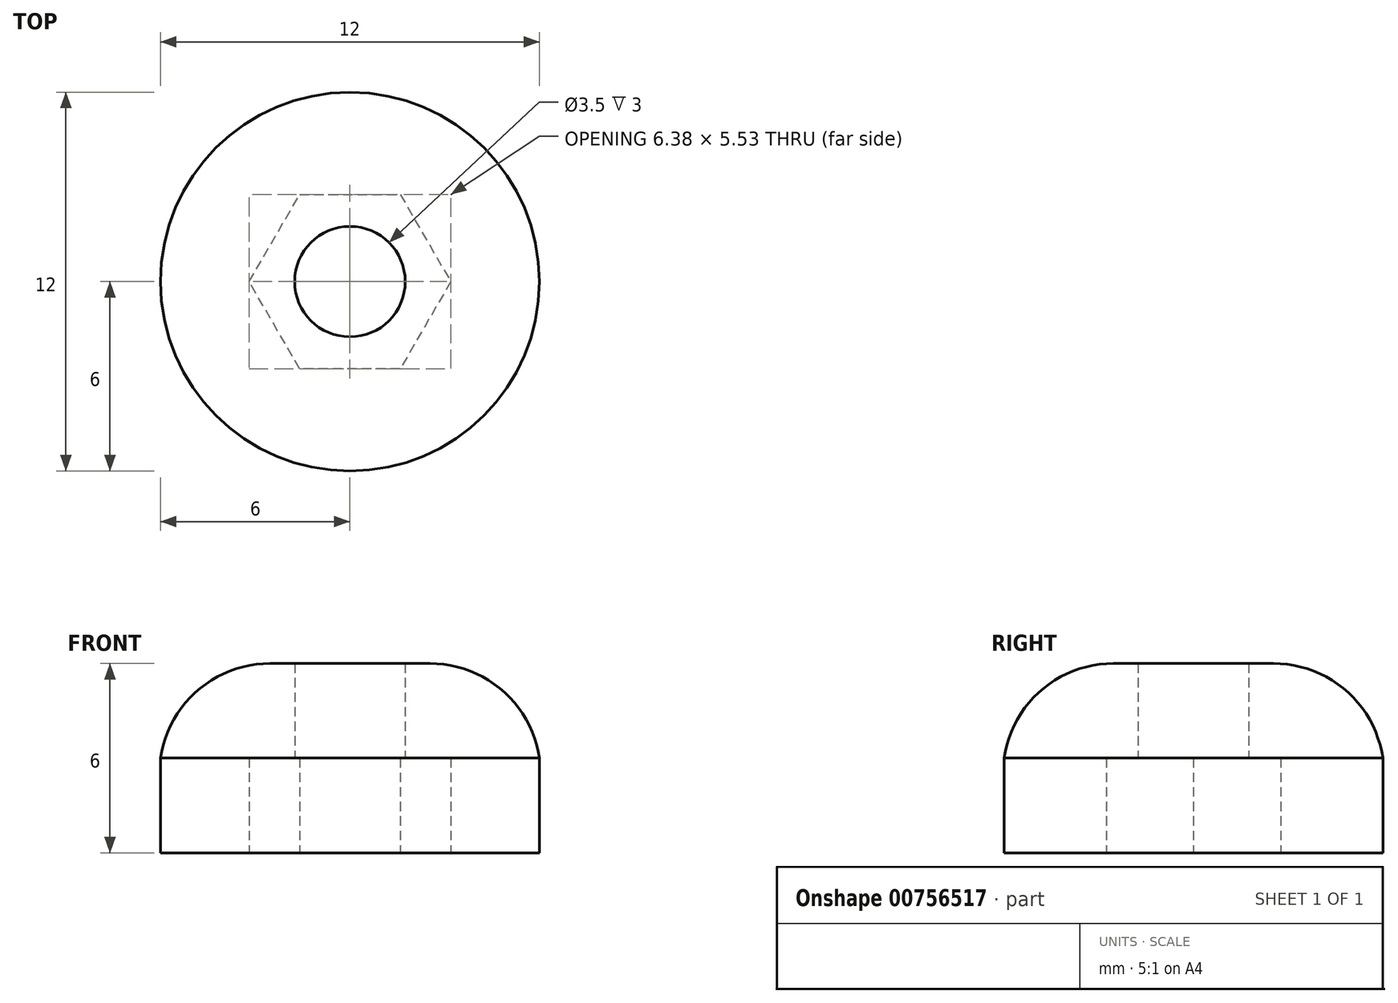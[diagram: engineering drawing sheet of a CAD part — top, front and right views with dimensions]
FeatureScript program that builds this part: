
annotation { "Feature Type Name" : "Feature", "Feature Type Description" : "" }
export const myFeature = defineFeature(function(context is Context, id is Id, definition is map)
    precondition{}
    {
        {
            var Q0;
            Q0=qCreatedBy(makeId("Top.planeOp"),FACE);
            var sketch = newSketch(context, id + "F0", { "sketchPlane" : qUnion([Q0])});
            skCircle(sketch, "E0", {"center": v(0, 0) * mm, "radius": 6 * mm});
            skCircle(sketch, "E1", {"center": v(0, 0) * mm, "radius": 2.75 * mm, "construction": true});
            skCircle(sketch, "E2.cCircle", {"center": v(0, 0) * mm, "radius": 3.2 * mm, "construction": true});
            skLineSegment(sketch, "E2.0", {"start": v(3.2, 0) * mm, "end": v(1.6, -2.76) * mm});
            skLineSegment(sketch, "E2.1", {"start": v(1.6, -2.76) * mm, "end": v(-1.6, -2.76) * mm});
            skLineSegment(sketch, "E2.2", {"start": v(-1.6, -2.76) * mm, "end": v(-3.2, 0) * mm});
            skLineSegment(sketch, "E2.3", {"start": v(-3.2, 0) * mm, "end": v(-1.6, 2.76) * mm});
            skLineSegment(sketch, "E2.4", {"start": v(-1.6, 2.76) * mm, "end": v(1.6, 2.76) * mm});
            skLineSegment(sketch, "E2.5", {"start": v(1.6, 2.76) * mm, "end": v(3.2, 0) * mm});
            skSolve(sketch);
        }
        {
            var Q0;
            Q0 = qSketchRegion(id + "F0", true);
            extrude(context, id + "F1", {"entities" : qUnion([Q0]), "depth" : 3 * mm, "offsetDistance" : 25 * mm});
        }
        {
            var Q0;
            Q0=qCreatedBy(makeId("Top.planeOp"),FACE);
            var sketch = newSketch(context, id + "F2", { "sketchPlane" : qUnion([Q0])});
            skCircle(sketch, "E3", {"center": v(0, 0) * mm, "radius": 6 * mm});
            skCircle(sketch, "E4", {"center": v(0, 0) * mm, "radius": 1.75 * mm});
            skSolve(sketch);
        }
        {
            var Q0;
            Q0 = qSketchRegion(id + "F2", true);
            extrude(context, id + "F3", {"entities" : qUnion([Q0]), "depth" : 3 * mm, "offsetDistance" : 25 * mm});
        }
        {
            var Q0;
            Q0=makeQuery(id+"F3.opExtrude","SWEPT_BODY",BODY,{"disambiguationData":[OSD([sQuery(id+"F2.wireOp",EDGE,"E3"),sQuery(id+"F2.wireOp",EDGE,"E4")])]});
            transform(context, id + "F4", {"entities" : qUnion([Q0]), "transformType" : TransformType.TRANSLATION_3D, "dx" : 0 * mm, "dy" : 0 * mm, "dz" : 3 * mm, "makeCopy" : false});
        }
        {
            var Q0;
            Q0=makeQuery(id+"F3.opExtrude","CAP_EDGE",EDGE,{"disambiguationData":[OSD([sQuery(id+"F2.wireOp",EDGE,"E3")])],"isStart":false});
            fillet(context, id + "F5", {"entities" : qUnion([Q0]), "radius" : 3.5 * mm, "tangentPropagation" : true, "allowEdgeOverflow" : false});
        }
    });
